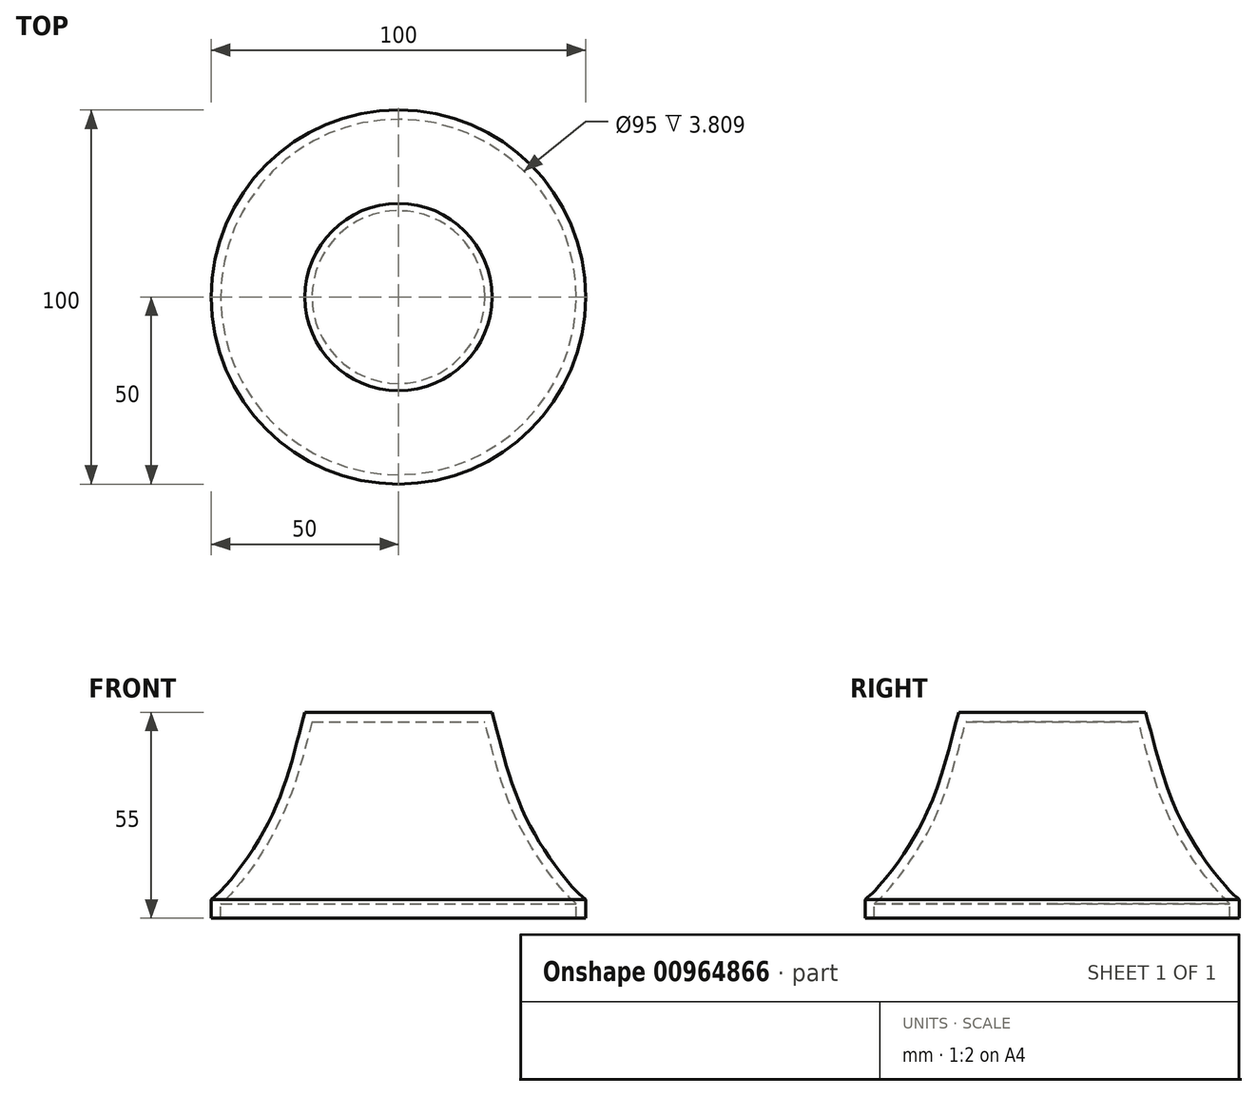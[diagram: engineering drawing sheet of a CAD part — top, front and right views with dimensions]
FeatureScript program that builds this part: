
annotation { "Feature Type Name" : "Feature", "Feature Type Description" : "" }
export const myFeature = defineFeature(function(context is Context, id is Id, definition is map)
    precondition{}
    {
        {
            var Q0;
            Q0=qCreatedBy(makeId("Front.planeOp"),FACE);
            var sketch = newSketch(context, id + "F0", { "sketchPlane" : qUnion([Q0])});
            skLineSegment(sketch, "E0", {"start": v(0, 50) * mm, "end": v(25, 50) * mm});
            skFitSpline(sketch, "E1", {"points": [v(25, 50) * mm, v(35, 20) * mm, v(50, 0) * mm], "startDerivative": vector(17.15, -64.6) * mm, "endDerivative": vector(25.5, -19.12) * mm});
            skLineSegment(sketch, "E2", {"start": v(50, 0) * mm, "end": v(0, 0) * mm});
            skLineSegment(sketch, "E3", {"start": v(0, 0) * mm, "end": v(0, 50) * mm});
            skSolve(sketch);
        }
        {
            var Q0;
            Q0=makeQuery(id+"F0.imprint","IMPRINT",FACE,{"disambiguationData":[TD([[makeQuery(id+"F0.imprint","IMPRINT",EDGE,{"derivedFrom":sQuery(id+"F0.wireOp",EDGE,"E0")}),-1.0]])]});
            var Q1;
            Q1=sQuery(id+"F0.wireOp",EDGE,"E3");
            revolve(context, id + "F1", {"surfaceOperationType" : NewSurfaceOperationType.NEW, "entities" : qUnion([Q0]), "axis" : qUnion([Q1]), "revolveType" : RevolveType.FULL});
        }
        {
            var Q0;
            Q0=makeQuery(id+"F1.opRevolve","SWEPT_FACE",FACE,{"disambiguationData":[OSD([sQuery(id+"F0.wireOp",EDGE,"E2")])]});
            var sketch = newSketch(context, id + "F2", { "sketchPlane" : qUnion([Q0])});
            skCircle(sketch, "E4.0.0", {"center": v(0, 0) * mm, "radius": 50 * mm});
            skSolve(sketch);
        }
        {
            var Q0;
            Q0=makeQuery(id+"F2.imprint","IMPRINT",FACE,{"disambiguationData":[TD([[makeQuery(id+"F2.imprint","IMPRINT",EDGE,{"derivedFrom":sQuery(id+"F2.wireOp",EDGE,"E4.0.0")}),1.0]])]});
            extrude(context, id + "F3", {"entities" : qUnion([Q0]), "operationType" : NewBodyOperationType.ADD, "depth" : 5 * mm, "offsetDistance" : 25 * mm});
        }
        {
            var Q0;
            Q0=makeQuery(id+"F3.opExtrude","CAP_FACE",FACE,{"disambiguationData":[OSD([sQuery(id+"F2.wireOp",EDGE,"E4.0.0")])],"isStart":false});
            shell(context, id + "F4", {"entities" : qUnion([Q0]), "thickness" : 2.5 * mm});
        }
    });
